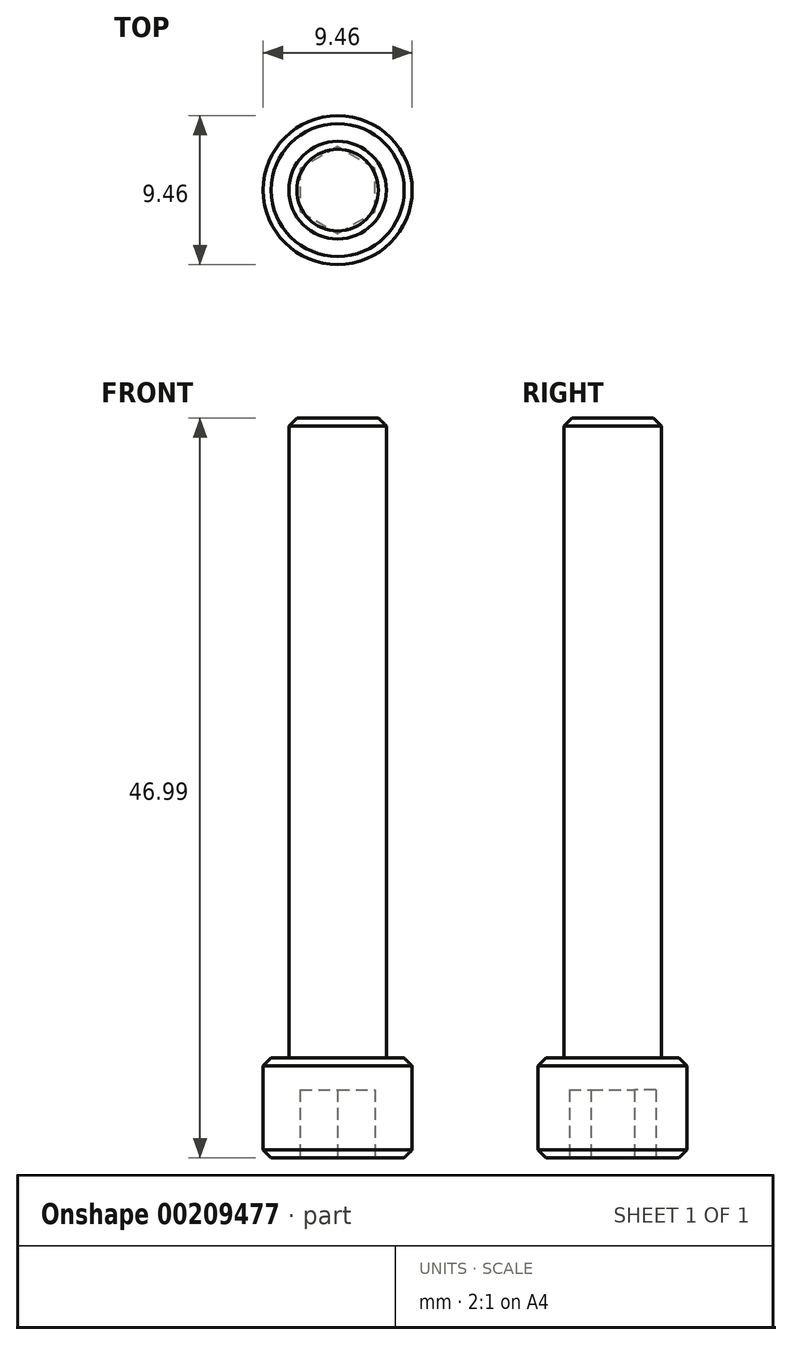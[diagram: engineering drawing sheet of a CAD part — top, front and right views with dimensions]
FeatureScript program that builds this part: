
annotation { "Feature Type Name" : "Feature", "Feature Type Description" : "" }
export const myFeature = defineFeature(function(context is Context, id is Id, definition is map)
    precondition{}
    {
        {
            var Q0;
            Q0=qCreatedBy(makeId("Top.planeOp"),FACE);
            var sketch = newSketch(context, id + "F0", { "sketchPlane" : qUnion([Q0])});
            skCircle(sketch, "E0", {"center": v(0, 0) * mm, "radius": 4.73 * mm});
            skSolve(sketch);
        }
        {
            var Q0;
            Q0 = qSketchRegion(id + "F0", true);
            extrude(context, id + "F1", {"entities" : qUnion([Q0]), "depth" : 6.35 * mm});
        }
        {
            var Q0;
            Q0=makeQuery(id+"F1.opExtrude","CAP_FACE",FACE,{"disambiguationData":[OSD([sQuery(id+"F0.wireOp",EDGE,"E0")])],"isStart":false});
            var sketch = newSketch(context, id + "F2", { "sketchPlane" : qUnion([Q0])});
            skCircle(sketch, "E1", {"center": v(0, 0) * mm, "radius": 3.1 * mm});
            skSolve(sketch);
        }
        {
            var Q0;
            Q0 = qSketchRegion(id + "F2", true);
            extrude(context, id + "F3", {"entities" : qUnion([Q0]), "operationType" : NewBodyOperationType.ADD, "depth" : 40.64 * mm});
        }
        {
            var Q0;
            Q0=makeQuery(id+"F1.opExtrude","CAP_FACE",FACE,{"disambiguationData":[OSD([sQuery(id+"F0.wireOp",EDGE,"E0")])],"isStart":true});
            var sketch = newSketch(context, id + "F4", { "sketchPlane" : qUnion([Q0])});
            skCircle(sketch, "E2.cCircle", {"center": v(0, 0) * mm, "radius": 2.38 * mm, "construction": true});
            skLineSegment(sketch, "E2.0", {"start": v(2.38, 1.37) * mm, "end": v(2.38, -1.37) * mm});
            skLineSegment(sketch, "E2.1", {"start": v(2.38, -1.37) * mm, "end": v(0, -2.75) * mm});
            skLineSegment(sketch, "E2.2", {"start": v(0, -2.75) * mm, "end": v(-2.38, -1.37) * mm});
            skLineSegment(sketch, "E2.3", {"start": v(-2.38, -1.37) * mm, "end": v(-2.38, 1.37) * mm});
            skLineSegment(sketch, "E2.4", {"start": v(-2.38, 1.37) * mm, "end": v(0, 2.75) * mm});
            skLineSegment(sketch, "E2.5", {"start": v(0, 2.75) * mm, "end": v(2.38, 1.37) * mm});
            skPoint(sketch, "E2.0.midPoint", {"position": v(2.38, 0) * mm});
            skSolve(sketch);
        }
        {
            var Q0;
            Q0 = qSketchRegion(id + "F4", true);
            extrude(context, id + "F5", {"entities" : qUnion([Q0]), "operationType" : NewBodyOperationType.REMOVE, "oppositeDirection" : true, "depth" : 4.32 * mm});
        }
        {
            var Q0;
            Q0=makeQuery(id+"F5.boolean.opBoolean","COPY",EDGE,{"derivedFrom":makeQuery(id+"F5.opExtrude","CAP_EDGE",EDGE,{"disambiguationData":[OSD([sQuery(id+"F4.wireOp",EDGE,"E2.1")])],"isStart":true})});
            var Q1;
            Q1=makeQuery(id+"F5.boolean.opBoolean","COPY",EDGE,{"derivedFrom":makeQuery(id+"F5.opExtrude","CAP_EDGE",EDGE,{"disambiguationData":[OSD([sQuery(id+"F4.wireOp",EDGE,"E2.0")])],"isStart":true})});
            var Q2;
            Q2=makeQuery(id+"F5.boolean.opBoolean","COPY",EDGE,{"derivedFrom":makeQuery(id+"F5.opExtrude","CAP_EDGE",EDGE,{"disambiguationData":[OSD([sQuery(id+"F4.wireOp",EDGE,"E2.5")])],"isStart":true})});
            var Q3;
            Q3=makeQuery(id+"F5.boolean.opBoolean","COPY",EDGE,{"derivedFrom":makeQuery(id+"F5.opExtrude","CAP_EDGE",EDGE,{"disambiguationData":[OSD([sQuery(id+"F4.wireOp",EDGE,"E2.4")])],"isStart":true})});
            var Q4;
            Q4=makeQuery(id+"F5.boolean.opBoolean","COPY",EDGE,{"derivedFrom":makeQuery(id+"F5.opExtrude","CAP_EDGE",EDGE,{"disambiguationData":[OSD([sQuery(id+"F4.wireOp",EDGE,"E2.3")])],"isStart":true})});
            var Q5;
            Q5=makeQuery(id+"F5.boolean.opBoolean","COPY",EDGE,{"derivedFrom":makeQuery(id+"F5.opExtrude","CAP_EDGE",EDGE,{"disambiguationData":[OSD([sQuery(id+"F4.wireOp",EDGE,"E2.2")])],"isStart":true})});
            var Q6;
            Q6=makeQuery(id+"F1.opExtrude","CAP_EDGE",EDGE,{"disambiguationData":[OSD([sQuery(id+"F0.wireOp",EDGE,"E0")])],"isStart":true});
            var Q7;
            Q7=makeQuery(id+"F1.opExtrude","CAP_EDGE",EDGE,{"disambiguationData":[OSD([sQuery(id+"F0.wireOp",EDGE,"E0")])],"isStart":false});
            var Q8;
            Q8=makeQuery(id+"F3.opExtrude","CAP_EDGE",EDGE,{"disambiguationData":[OSD([sQuery(id+"F2.wireOp",EDGE,"E1")])],"isStart":false});
            chamfer(context, id + "F6", {"entities" : qUnion([Q0, Q1, Q2, Q3, Q4, Q5, Q6, Q7, Q8]), "width" : 0.5 * mm, "tangentPropagation" : true});
        }
    });
